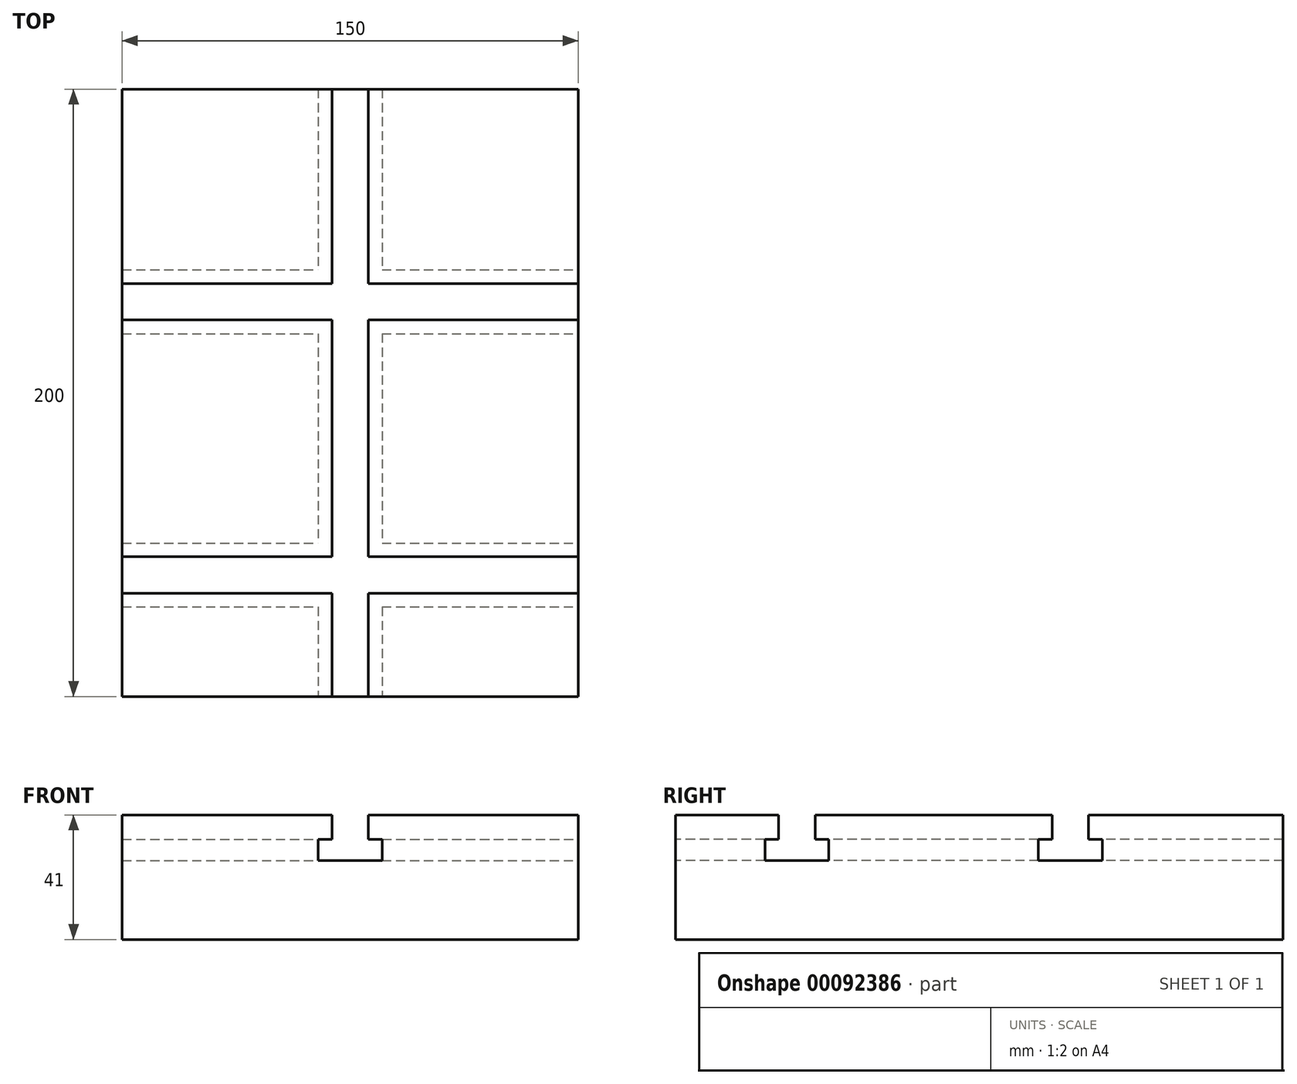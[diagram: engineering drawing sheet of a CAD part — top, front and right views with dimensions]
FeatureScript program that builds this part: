
annotation { "Feature Type Name" : "Feature", "Feature Type Description" : "" }
export const myFeature = defineFeature(function(context is Context, id is Id, definition is map)
    precondition{}
    {
        {
            var Q0;
            Q0=qCreatedBy(makeId("Front.planeOp"),FACE);
            var sketch = newSketch(context, id + "F0", { "sketchPlane" : qUnion([Q0])});
            skLineSegment(sketch, "E0.bottom", {"start": v(-75, 0) * mm, "end": v(75, 0) * mm});
            skLineSegment(sketch, "E0.top", {"start": v(-75, -41) * mm, "end": v(75, -41) * mm});
            skLineSegment(sketch, "E0.left", {"start": v(-75, 0) * mm, "end": v(-75, -41) * mm});
            skLineSegment(sketch, "E0.right", {"start": v(75, 0) * mm, "end": v(75, -41) * mm});
            skSolve(sketch);
        }
        {
            var Q0;
            Q0=makeQuery(id+"F0.imprint","IMPRINT",FACE,{"disambiguationData":[TD([[makeQuery(id+"F0.imprint","IMPRINT",EDGE,{"derivedFrom":sQuery(id+"F0.wireOp",EDGE,"E0.bottom")}),-1.0]])]});
            extrude(context, id + "F1", {"entities" : qUnion([Q0]), "endBound" : BoundingType.SYMMETRIC, "oppositeDirection" : true, "depth" : 200 * mm});
        }
        {
            var Q0;
            Q0=makeQuery(id+"F1.opExtrude","CAP_FACE",FACE,{"disambiguationData":[OSD([sQuery(id+"F0.wireOp",EDGE,"E0.bottom"),sQuery(id+"F0.wireOp",EDGE,"E0.top"),sQuery(id+"F0.wireOp",EDGE,"E0.left"),sQuery(id+"F0.wireOp",EDGE,"E0.right")])],"isStart":true});
            var sketch = newSketch(context, id + "F2", { "sketchPlane" : qUnion([Q0])});
            skLineSegment(sketch, "E1", {"start": v(-6, 0) * mm, "end": v(-6, -8) * mm});
            skLineSegment(sketch, "E2", {"start": v(-6, -8) * mm, "end": v(-10.5, -8) * mm});
            skLineSegment(sketch, "E3", {"start": v(-10.5, -8) * mm, "end": v(-10.5, -15) * mm});
            skLineSegment(sketch, "E4", {"start": v(-10.5, -15) * mm, "end": v(10.5, -15) * mm});
            skLineSegment(sketch, "E5", {"start": v(10.5, -15) * mm, "end": v(10.5, -8) * mm});
            skLineSegment(sketch, "E6", {"start": v(10.5, -8) * mm, "end": v(6, -8) * mm});
            skLineSegment(sketch, "E7", {"start": v(6, -8) * mm, "end": v(6, 0) * mm});
            skLineSegment(sketch, "E8", {"start": v(6, 0) * mm, "end": v(-6, 0) * mm});
            skSolve(sketch);
        }
        {
            var Q0;
            Q0=makeQuery(id+"F2.imprint","IMPRINT",FACE,{"disambiguationData":[TD([[makeQuery(id+"F2.imprint","IMPRINT",EDGE,{"derivedFrom":sQuery(id+"F2.wireOp",EDGE,"E1")}),1.0]])]});
            extrude(context, id + "F3", {"entities" : qUnion([Q0]), "operationType" : NewBodyOperationType.REMOVE, "endBound" : BoundingType.THROUGH_ALL, "oppositeDirection" : true, "depth" : 25 * mm});
        }
        {
            var Q0;
            Q0=makeQuery(id+"F1.opExtrude","SWEPT_FACE",FACE,{"disambiguationData":[OSD([sQuery(id+"F0.wireOp",EDGE,"E0.right")])]});
            var sketch = newSketch(context, id + "F4", { "sketchPlane" : qUnion([Q0])});
            skLineSegment(sketch, "E9", {"start": v(-66, 0) * mm, "end": v(-66, -8) * mm});
            skLineSegment(sketch, "E10", {"start": v(-66, -8) * mm, "end": v(-70.5, -8) * mm});
            skLineSegment(sketch, "E11", {"start": v(-70.5, -8) * mm, "end": v(-70.5, -15) * mm});
            skLineSegment(sketch, "E12", {"start": v(-70.5, -15) * mm, "end": v(-49.5, -15) * mm});
            skLineSegment(sketch, "E13", {"start": v(-49.5, -15) * mm, "end": v(-49.5, -8) * mm});
            skLineSegment(sketch, "E14", {"start": v(-49.5, -8) * mm, "end": v(-54, -8) * mm});
            skLineSegment(sketch, "E15", {"start": v(-54, -8) * mm, "end": v(-54, 0) * mm});
            skLineSegment(sketch, "E16", {"start": v(-54, 0) * mm, "end": v(-66, 0) * mm});
            skLineSegment(sketch, "E17", {"start": v(24, 0) * mm, "end": v(24, -8) * mm});
            skLineSegment(sketch, "E18", {"start": v(24, -8) * mm, "end": v(19.5, -8) * mm});
            skLineSegment(sketch, "E19", {"start": v(19.5, -8) * mm, "end": v(19.5, -15) * mm});
            skLineSegment(sketch, "E20", {"start": v(19.5, -15) * mm, "end": v(40.5, -15) * mm});
            skLineSegment(sketch, "E21", {"start": v(40.5, -15) * mm, "end": v(40.5, -8) * mm});
            skLineSegment(sketch, "E22", {"start": v(40.5, -8) * mm, "end": v(36, -8) * mm});
            skLineSegment(sketch, "E23", {"start": v(36, -8) * mm, "end": v(36, 0) * mm});
            skLineSegment(sketch, "E24", {"start": v(36, 0) * mm, "end": v(24, 0) * mm});
            skSolve(sketch);
        }
        {
            var Q0;
            Q0=makeQuery(id+"F4.imprint","IMPRINT",FACE,{"disambiguationData":[TD([[makeQuery(id+"F4.imprint","IMPRINT",EDGE,{"derivedFrom":sQuery(id+"F4.wireOp",EDGE,"E9")}),1.0]])]});
            var Q1;
            Q1=makeQuery(id+"F4.imprint","IMPRINT",FACE,{"disambiguationData":[TD([[makeQuery(id+"F4.imprint","IMPRINT",EDGE,{"derivedFrom":sQuery(id+"F4.wireOp",EDGE,"E17")}),1.0]])]});
            extrude(context, id + "F5", {"entities" : qUnion([Q0, Q1]), "operationType" : NewBodyOperationType.REMOVE, "endBound" : BoundingType.THROUGH_ALL, "oppositeDirection" : true, "depth" : 25 * mm});
        }
    });
